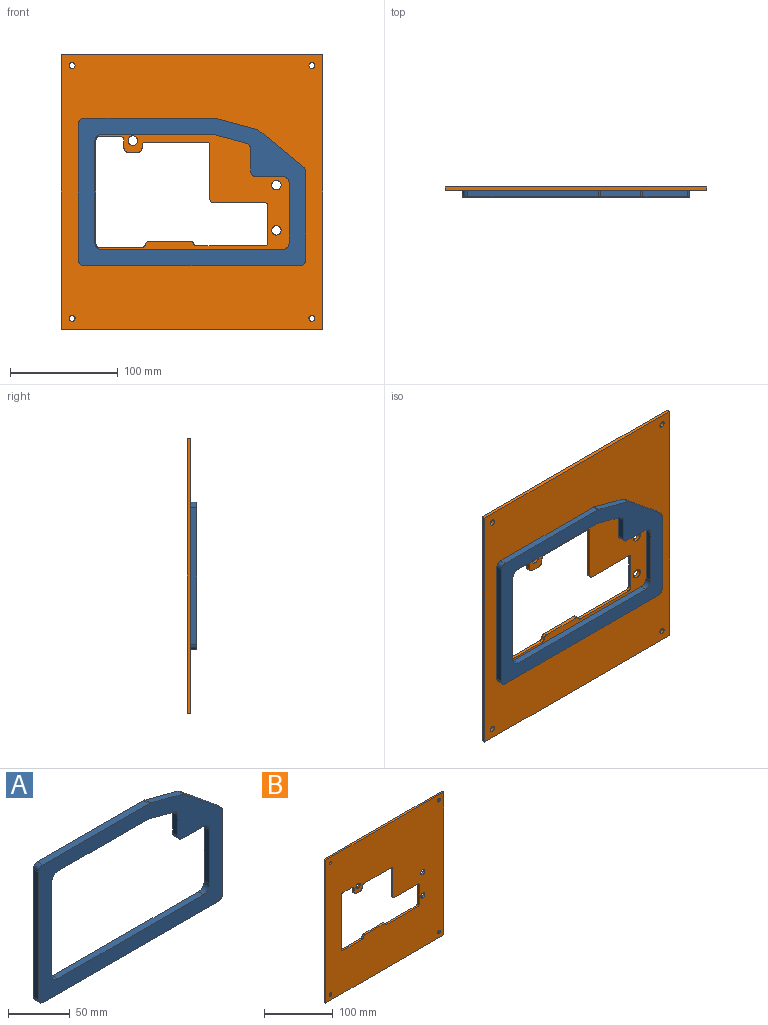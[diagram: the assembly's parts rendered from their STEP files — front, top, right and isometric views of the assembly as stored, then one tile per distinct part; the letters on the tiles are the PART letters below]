
ASSEMBLY  parts=2 mates=1
PART A: 28 faces, bbox 211.2x6x137 mm
  f0: plane 211.2x137mm, normal (0,-1,0), area 9659.8mm2, adj f2,f3,f4,f5,f6,f7,f8,f9
  f1: plane 211.2x137mm, normal (0,1,0), area 9659.8mm2, adj f2,f3,f4,f5,f6,f7,f8,f9
  f2: plane 54x6mm, normal (-1,0,0), area 324mm2, adj f0,f1,f9,f11
  f3: plane 24.2x6mm, normal (0,0,-1), area 145.2mm2, adj f0,f1,f9,f13
  f4: plane 20.92x6mm, normal (-1,0,0), area 125.5mm2, adj f0,f1,f13,f14
  f5: plane 30.17x8.08mm, normal (-0.26,0,-0.97), area 187.4mm2, adj f0,f1,f14,f15
  f6: plane 102.83x6mm, normal (0,0,-1), area 617mm2, adj f0,f1,f12,f15
  f7: plane 93x6mm, normal (1,0,0), area 558mm2, adj f0,f1,f10,f12
  f8: plane 167.2x6mm, normal (0,0,1), area 1003.2mm2, adj f0,f1,f10,f11
  f9: cylinder r=7mm len=7mm, axis (0,1,0), area 66mm2, adj f0,f1,f2,f3
  f10: cylinder r=7mm len=7mm, axis (0,1,0), area 66mm2, adj f0,f1,f7,f8
  f11: cylinder r=7mm len=7mm, axis (0,-1,0), area 66mm2, adj f0,f1,f2,f8
  f12: cylinder r=7mm len=7mm, axis (0,-1,0), area 66mm2, adj f0,f1,f6,f7
  f13: cylinder r=5mm len=6mm, axis (0,1,0), area 47.1mm2, adj f0,f1,f3,f4
  f14: cylinder r=5mm len=6mm, axis (0,1,0), area 39.3mm2, adj f0,f1,f4,f5
  f15: cylinder r=5mm len=6mm, axis (0,-1,0), area 7.9mm2, adj f0,f1,f5,f6
  f16: plane 127x6mm, normal (-1,0,0), area 762mm2, adj f0,f1,f22,f27
  f17: plane 121.81x6mm, normal (0,0,1), area 730.8mm2, adj f0,f1,f22,f23
  f18: plane 37.87x10.15mm, normal (0.26,0,0.97), area 235.2mm2, adj f0,f1,f23,f24
  f19: plane 41.52x34.13mm, normal (0.63,0,0.77), area 322.5mm2, adj f0,f1,f24,f25
  f20: plane 82.73x6mm, normal (1,0,0), area 496.4mm2, adj f0,f1,f25,f26
  f21: plane 201.2x6mm, normal (0,0,-1), area 1207.2mm2, adj f0,f1,f26,f27
  f22: cylinder r=5mm len=6mm, axis (0,-1,0), area 47.1mm2, adj f0,f1,f16,f17
  f23: cylinder r=5mm len=6mm, axis (0,-1,0), area 7.9mm2, adj f0,f1,f17,f18
  f24: cylinder r=5mm len=6mm, axis (0,-1,0), area 12.8mm2, adj f0,f1,f18,f19
  f25: cylinder r=5mm len=6mm, axis (0,-1,0), area 26.5mm2, adj f0,f1,f19,f20
  f26: cylinder r=5mm len=6mm, axis (0,-1,0), area 47.1mm2, adj f0,f1,f20,f21
  f27: cylinder r=5mm len=6mm, axis (0,-1,0), area 47.1mm2, adj f0,f1,f16,f21
PART B: 41 faces, bbox 243x3.2x255 mm
  f0: plane 243x3.18mm, normal (0,0,-1), area 771.5mm2, adj f2,f3,f35,f36
  f1: plane 243x3.18mm, normal (0,0,1), area 771.5mm2, adj f2,f3,f35,f36
  f2: plane 255x243mm, normal (0,-1,0), area 49457.8mm2, adj f0,f1,f4,f5,f6,f7,f8,f9
  f3: plane 255x243mm, normal (0,1,0), area 49457.8mm2, adj f0,f1,f4,f5,f6,f7,f8,f9
  f4: plane 63.14x3.18mm, normal (0,0,1), area 200.5mm2, adj f2,f3,f26,f34
  f5: plane 34.11x3.18mm, normal (-1,0,0), area 108.3mm2, adj f2,f3,f26,f27
  f6: plane 48x3.18mm, normal (0,0,-1), area 152.4mm2, adj f2,f3,f20,f27
  f7: plane 50.4x3.18mm, normal (-1,0,0), area 160mm2, adj f2,f3,f20,f21
  f8: plane 57x3.18mm, normal (0,0,-1), area 181mm2, adj f2,f3,f21,f22
  f9: plane 3.18x2mm, normal (1,0,0), area 6.3mm2, adj f2,f3,f18,f22
  f10: plane 7x3.18mm, normal (0,0,-1), area 22.2mm2, adj f2,f3,f18,f19
  f11: plane 7x3.18mm, normal (-1,0,0), area 22.2mm2, adj f2,f3,f19,f23
  f12: plane 20x3.18mm, normal (0,0,-1), area 63.5mm2, adj f2,f3,f23,f24
  f13: plane 96.75x3.18mm, normal (1,0,0), area 307.2mm2, adj f2,f3,f24,f25
  f14: plane 40.14x3.18mm, normal (0,0,1), area 127.4mm2, adj f2,f3,f25,f31
  f15: plane 3.18x0.07mm, normal (-0.99,0,0.14), area 0.2mm2, adj f2,f3,f31,f32
  f16: plane 39.11x3.18mm, normal (0,0,1), area 124.2mm2, adj f2,f3,f32,f33
  f17: plane 3.18x0.03mm, normal (0.94,0,0.34), area 0.1mm2, adj f2,f3,f33,f34
  f18: cylinder r=5mm len=5mm, axis (0,-1,0), area 24.9mm2, adj f2,f3,f9,f10
  f19: cylinder r=5mm len=5mm, axis (0,-1,0), area 24.9mm2, adj f2,f3,f10,f11
  f20: cylinder r=3mm len=3.18mm, axis (0,-1,0), area 15mm2, adj f2,f3,f6,f7
  f21: cylinder r=3mm len=3.18mm, axis (0,1,0), area 15mm2, adj f2,f3,f7,f8
  f22: cylinder r=3mm len=3.18mm, axis (0,-1,0), area 15mm2, adj f2,f3,f8,f9
  f23: cylinder r=3mm len=3.18mm, axis (0,-1,0), area 15mm2, adj f2,f3,f11,f12
  f24: cylinder r=3mm len=3.18mm, axis (0,-1,0), area 15mm2, adj f2,f3,f12,f13
  f25: cylinder r=3mm len=3.18mm, axis (0,1,0), area 15mm2, adj f2,f3,f13,f14
  f26: cylinder r=3mm len=3.18mm, axis (0,-1,0), area 15mm2, adj f2,f3,f4,f5
  f27: cylinder r=3mm len=3.18mm, axis (0,1,0), area 15mm2, adj f2,f3,f5,f6
  f28: cylinder r=4.38mm len=8.75mm, axis (0,-1,0), area 87.3mm2, adj f2,f3
  f29: cylinder r=4.38mm len=8.75mm, axis (0,-1,0), area 87.3mm2, adj f2,f3
  f30: cylinder r=4.38mm len=8.75mm, axis (0,-1,0), area 87.3mm2, adj f2,f3
  f31: cylinder r=3mm len=3.18mm, axis (0,-1,0), area 13.7mm2, adj f2,f3,f14,f15
  f32: cylinder r=3mm len=3.18mm, axis (0,-1,0), area 13.7mm2, adj f2,f3,f15,f16
  f33: cylinder r=3mm len=3.18mm, axis (0,1,0), area 11.7mm2, adj f2,f3,f16,f17
  f34: cylinder r=3mm len=3.18mm, axis (0,1,0), area 11.7mm2, adj f2,f3,f4,f17
  f35: plane 255x3.18mm, normal (-1,0,0), area 809.6mm2, adj f0,f1,f2,f3
  f36: plane 255x3.18mm, normal (1,0,0), area 809.6mm2, adj f0,f1,f2,f3
  f37: cylinder r=2.75mm len=5.5mm, axis (0,-1,0), area 54.9mm2, adj f2,f3
  f38: cylinder r=2.75mm len=5.5mm, axis (0,-1,0), area 54.9mm2, adj f2,f3
  f39: cylinder r=2.75mm len=5.5mm, axis (0,-1,0), area 54.9mm2, adj f2,f3
  f40: cylinder r=2.75mm len=5.5mm, axis (0,-1,0), area 54.9mm2, adj f2,f3
PLACE A t=(-5.41,13.31,18.33)mm
PLACE B t=(-14.76,16.48,18.33)mm
MATE planar A.f1 <-> B.f2  axis (0,1,0) through (-6.71,13.31,15.85)mm
